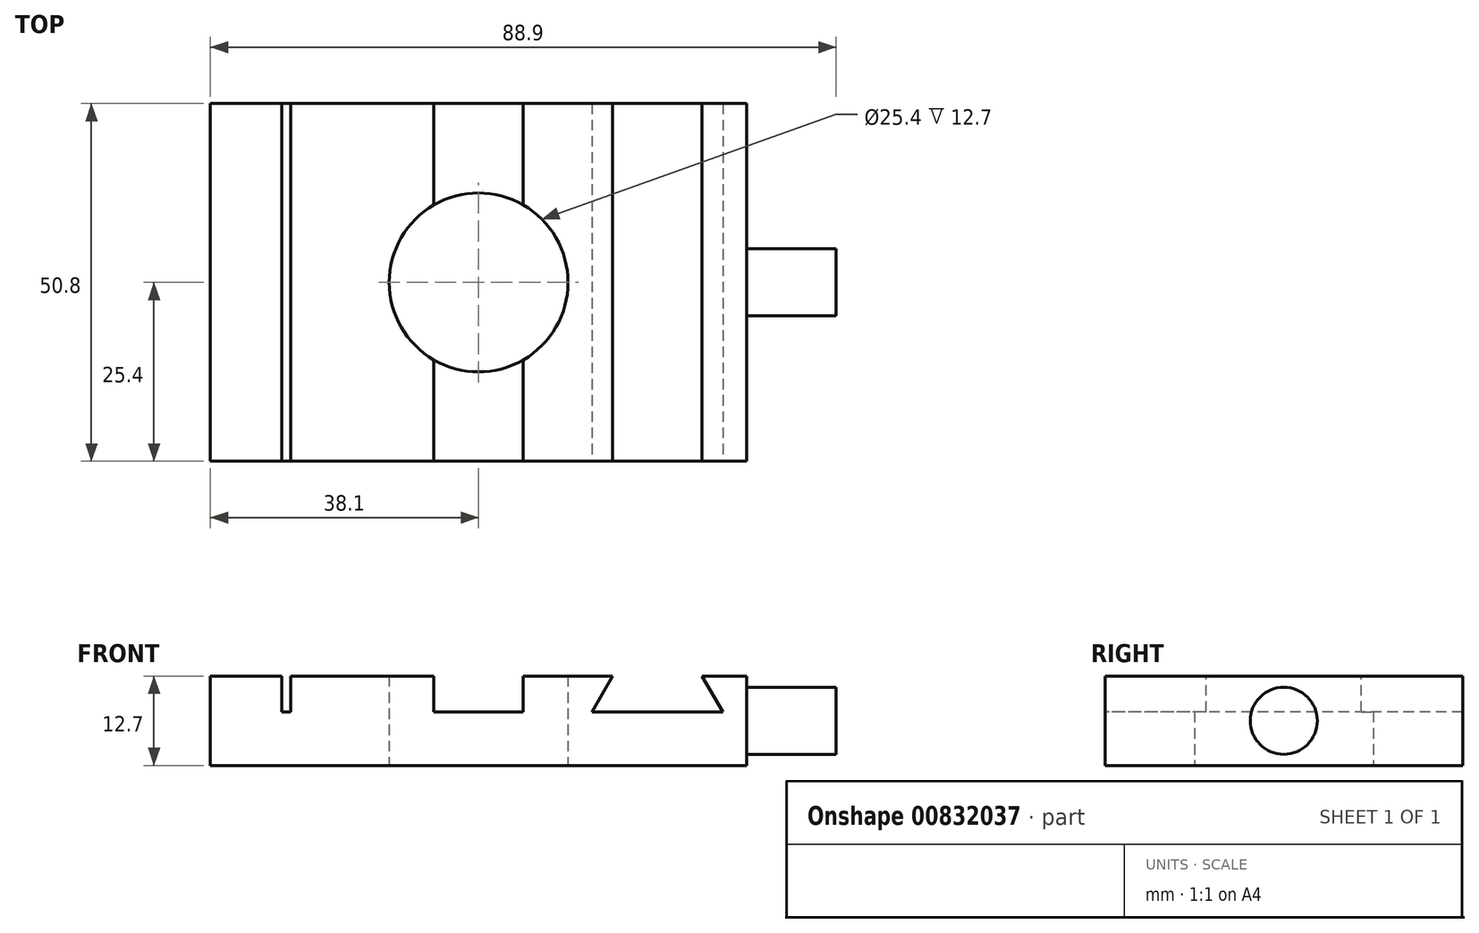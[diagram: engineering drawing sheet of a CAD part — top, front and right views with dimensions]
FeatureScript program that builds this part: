
annotation { "Feature Type Name" : "Feature", "Feature Type Description" : "" }
export const myFeature = defineFeature(function(context is Context, id is Id, definition is map)
    precondition{}
    {
        {
            var Q0;
            Q0=qCreatedBy(makeId("Top.planeOp"),FACE);
            var sketch = newSketch(context, id + "F0", { "sketchPlane" : qUnion([Q0])});
            skLineSegment(sketch, "E0.bottom", {"start": v(-38.1, -25.4) * mm, "end": v(38.1, -25.4) * mm});
            skLineSegment(sketch, "E0.top", {"start": v(-38.1, 25.4) * mm, "end": v(38.1, 25.4) * mm});
            skLineSegment(sketch, "E0.left", {"start": v(-38.1, -25.4) * mm, "end": v(-38.1, 25.4) * mm});
            skLineSegment(sketch, "E0.right", {"start": v(38.1, -25.4) * mm, "end": v(38.1, 25.4) * mm});
            skPoint(sketch, "E0.middle", {"position": v(0, 0) * mm});
            skCircle(sketch, "E1", {"center": v(0, 0) * mm, "radius": 12.7 * mm});
            skSolve(sketch);
        }
        {
            var Q0;
            Q0=makeQuery(id+"F0.imprint","IMPRINT",FACE,{"disambiguationData":[TD([[makeQuery(id+"F0.imprint","IMPRINT",EDGE,{"derivedFrom":sQuery(id+"F0.wireOp",EDGE,"E0.bottom")}),1.0]])]});
            extrude(context, id + "F1", {"entities" : qUnion([Q0]), "depth" : 12.7 * mm, "offsetDistance" : 25 * mm});
        }
        {
            var Q0;
            Q0=makeQuery(id+"F1.opExtrude","CAP_FACE",FACE,{"disambiguationData":[OSD([sQuery(id+"F0.wireOp",EDGE,"E0.bottom"),sQuery(id+"F0.wireOp",EDGE,"E0.top"),sQuery(id+"F0.wireOp",EDGE,"E0.left"),sQuery(id+"F0.wireOp",EDGE,"E0.right"),sQuery(id+"F0.wireOp",EDGE,"E1")])],"isStart":false});
            var sketch = newSketch(context, id + "F2", { "sketchPlane" : qUnion([Q0])});
            skLineSegment(sketch, "E2.bottom", {"start": v(-27.94, 25.4) * mm, "end": v(-26.67, 25.4) * mm});
            skLineSegment(sketch, "E2.top", {"start": v(-27.94, -25.4) * mm, "end": v(-26.67, -25.4) * mm});
            skLineSegment(sketch, "E2.left", {"start": v(-27.94, 25.4) * mm, "end": v(-27.94, -25.4) * mm});
            skLineSegment(sketch, "E2.right", {"start": v(-26.67, 25.4) * mm, "end": v(-26.67, -25.4) * mm});
            skLineSegment(sketch, "E3", {"start": v(-6.35, 25.4) * mm, "end": v(-6.35, -25.4) * mm});
            skLineSegment(sketch, "E4", {"start": v(-6.35, -25.4) * mm, "end": v(6.35, -25.4) * mm});
            skLineSegment(sketch, "E5", {"start": v(6.35, -25.4) * mm, "end": v(6.35, 25.4) * mm});
            skLineSegment(sketch, "E6", {"start": v(6.35, 25.4) * mm, "end": v(-6.35, 25.4) * mm});
            skPoint(sketch, "E7", {"position": v(0, 0) * mm});
            skLineSegment(sketch, "E8", {"start": v(0, 25.4) * mm, "end": v(0, -25.4) * mm, "construction": true});
            skSolve(sketch);
        }
        {
            var Q0;
            Q0=makeQuery(id+"F2.imprint","IMPRINT",FACE,{"disambiguationData":[TD([[makeQuery(id+"F2.imprint","IMPRINT",EDGE,{"derivedFrom":sQuery(id+"F2.wireOp",EDGE,"E2.bottom")}),-1.0]])]});
            var Q1;
            {var subQ0=sQuery(id+"F2.wireOp",EDGE,"E4");Q1=makeQuery(id+"F2.imprint","IMPRINT",FACE,{"disambiguationData":[TD([[makeQuery(id+"F2.imprint","IMPRINT",EDGE,{"derivedFrom":subQ0}),1.0]])]});}
            var Q2;
            {var subQ0=sQuery(id+"F2.wireOp",EDGE,"E6");Q2=makeQuery(id+"F2.imprint","IMPRINT",FACE,{"disambiguationData":[TD([[makeQuery(id+"F2.imprint","IMPRINT",EDGE,{"derivedFrom":subQ0}),-1.0]])]});}
            extrude(context, id + "F3", {"entities" : qUnion([Q0, Q1, Q2]), "operationType" : NewBodyOperationType.REMOVE, "oppositeDirection" : true, "depth" : 5.08 * mm, "offsetDistance" : 25 * mm});
        }
        {
            var Q0;
            Q0=makeQuery(id+"F1.opExtrude","SWEPT_FACE",FACE,{"disambiguationData":[OSD([sQuery(id+"F0.wireOp",EDGE,"E0.bottom")])]});
            var sketch = newSketch(context, id + "F4", { "sketchPlane" : qUnion([Q0])});
            skLineSegment(sketch, "E9", {"start": v(19.05, 12.7) * mm, "end": v(16.12, 7.62) * mm});
            skLineSegment(sketch, "E10", {"start": v(16.12, 7.62) * mm, "end": v(34.68, 7.62) * mm});
            skLineSegment(sketch, "E11", {"start": v(34.68, 7.62) * mm, "end": v(31.75, 12.7) * mm});
            skLineSegment(sketch, "E12", {"start": v(31.75, 12.7) * mm, "end": v(19.05, 12.7) * mm});
            skLineSegment(sketch, "E13", {"start": v(25.4, 7.62) * mm, "end": v(25.4, 12.7) * mm, "construction": true});
            skSolve(sketch);
        }
        {
            var Q0;
            Q0 = qSketchRegion(id + "F4", true);
            extrude(context, id + "F5", {"entities" : qUnion([Q0]), "operationType" : NewBodyOperationType.REMOVE, "endBound" : BoundingType.THROUGH_ALL, "oppositeDirection" : true, "depth" : 25 * mm, "offsetDistance" : 25 * mm});
        }
        {
            var Q0;
            Q0=makeQuery(id+"F1.opExtrude","SWEPT_FACE",FACE,{"disambiguationData":[OSD([sQuery(id+"F0.wireOp",EDGE,"E0.right")])]});
            var sketch = newSketch(context, id + "F6", { "sketchPlane" : qUnion([Q0])});
            skCircle(sketch, "E14", {"center": v(0, 6.35) * mm, "radius": 4.76 * mm});
            skPoint(sketch, "E14.centerSnap0", {"position": v(-25.4, 6.35) * mm});
            skPoint(sketch, "E14.centerSnap1", {"position": v(0, 12.7) * mm});
            skSolve(sketch);
        }
        {
            var Q0;
            Q0 = qSketchRegion(id + "F6", true);
            extrude(context, id + "F7", {"entities" : qUnion([Q0]), "operationType" : NewBodyOperationType.ADD, "depth" : 12.7 * mm, "offsetDistance" : 25 * mm});
        }
    });
